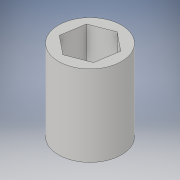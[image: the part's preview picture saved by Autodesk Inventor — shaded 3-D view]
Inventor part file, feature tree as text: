
AUTODESK INVENTOR PART (.ipt)
format: ipt  version: 2019 (Build 230136000, 136)  size: 97,792 bytes
history: native  units: in
note: dims shown in document units (in); Inventor stores cm internally (conversion verified against a paired STEP export)
features: extrude x1, sketch x1
ambient origin geometry x8: Origin, YZ Plane, XZ Plane, XY Plane, X Axis, Y Axis, Z Axis, Center Point
bodies: Solid1 (feature_tree)
feature tree (2):
  extrude  "Extrusion1"  Depth=1.0in TaperAngle=0.0deg
  sketch  "Sketch1"  dims[d0=0.29in d1=1.0in d2=0.0in]
